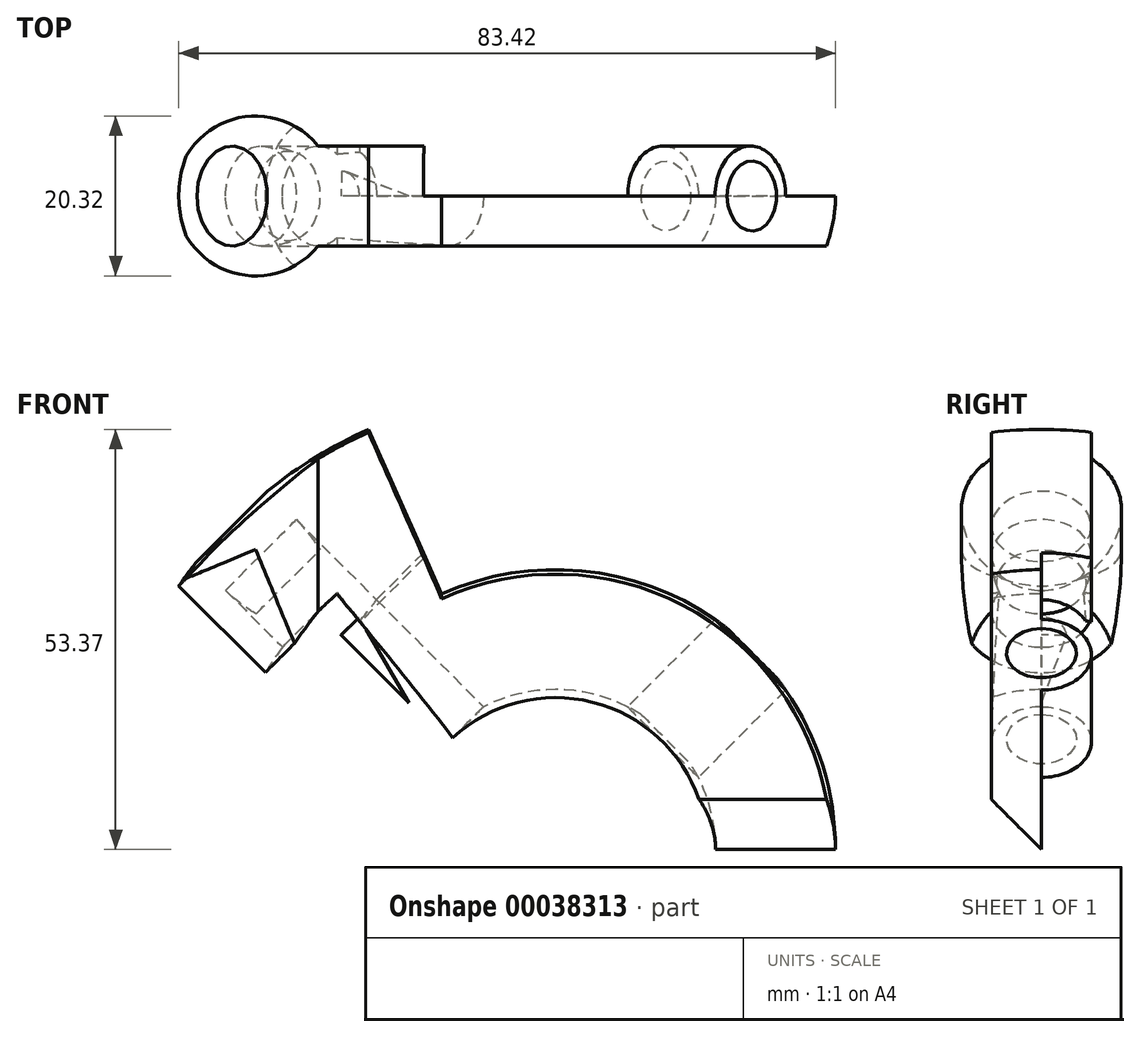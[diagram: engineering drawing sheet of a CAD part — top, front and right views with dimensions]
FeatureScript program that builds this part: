
annotation { "Feature Type Name" : "Feature", "Feature Type Description" : "" }
export const myFeature = defineFeature(function(context is Context, id is Id, definition is map)
    precondition{}
    {
        {
            var Q0;
            Q0=qCreatedBy(makeId("Front.planeOp"),FACE);
            var sketch = newSketch(context, id + "F0", { "sketchPlane" : qUnion([Q0])});
            skArc(sketch, "E0", {"start": v(-26.92, 43.08) * mm, "mid": v(-44.43, 24.63) * mm, "end": v(-50.8, 0) * mm});
            skArc(sketch, "E1.0", {"start": v(-23.76, 53.37) * mm, "mid": v(-49, 31.82) * mm, "end": v(-58.42, 0) * mm});
            skLineSegment(sketch, "E2", {"start": v(-36.32, 0) * mm, "end": v(-50.8, 0) * mm, "construction": true});
            skLineSegment(sketch, "E3", {"start": v(-50.8, 0) * mm, "end": v(48.72, 0) * mm, "construction": true});
            skLineSegment(sketch, "E4", {"start": v(-58.42, 0) * mm, "end": v(-50.8, 0) * mm});
            skLineSegment(sketch, "E5", {"start": v(50.8, 0) * mm, "end": v(58.42, 0) * mm});
            skLineSegment(sketch, "E6", {"start": v(0, 0) * mm, "end": v(0, 35.62) * mm, "construction": true});
            skLineSegment(sketch, "E7", {"start": v(-23.76, 53.37) * mm, "end": v(-14.46, 32.49) * mm});
            skLineSegment(sketch, "E8", {"start": v(-26.92, 43.08) * mm, "end": v(-14.8, 23.7) * mm});
            skArc(sketch, "E9", {"start": v(35.56, 0) * mm, "mid": v(19.37, 29.82) * mm, "end": v(-14.46, 32.49) * mm});
            skArc(sketch, "E10.0", {"start": v(27.94, 0) * mm, "mid": v(13.55, 24.44) * mm, "end": v(-14.8, 23.7) * mm});
            skLineSegment(sketch, "E11", {"start": v(27.94, 0) * mm, "end": v(35.56, 0) * mm});
            skSolve(sketch);
        }
        {
            var Q0;
            Q0=makeQuery(id+"F0.imprint","IMPRINT",FACE,{"disambiguationData":[TD([[makeQuery(id+"F0.imprint","IMPRINT",EDGE,{"derivedFrom":sQuery(id+"F0.wireOp",EDGE,"E0")}),-1.0]])]});
            var Q1;
            Q1=sQuery(id+"F0.wireOp",EDGE,"E3");
            revolve(context, id + "F1", {"entities" : qUnion([Q0]), "axis" : qUnion([Q1]), "revolveType" : RevolveType.SYMMETRIC, "angle" : 90 * degree});
        }
        {
            var Q0;
            Q0=qCreatedBy(makeId("Front.planeOp"),FACE);
            var sketch = newSketch(context, id + "F2", { "sketchPlane" : qUnion([Q0])});
            skArc(sketch, "E12", {"start": v(50.8, 0) * mm, "mid": v(46.93, 19.44) * mm, "end": v(35.92, 35.92) * mm, "construction": true});
            skArc(sketch, "E13.0", {"start": v(43.18, 0) * mm, "mid": v(39.9, 16.52) * mm, "end": v(30.53, 30.53) * mm, "construction": true});
            skLineSegment(sketch, "E14", {"start": v(-50.8, 0) * mm, "end": v(-43.18, 0) * mm});
            skLineSegment(sketch, "E15", {"start": v(43.18, 0) * mm, "end": v(50.8, 0) * mm, "construction": true});
            skLineSegment(sketch, "E16", {"start": v(0, 0) * mm, "end": v(-43.18, 0) * mm, "construction": true});
            skLineSegment(sketch, "E17", {"start": v(0, 0) * mm, "end": v(-64.06, 64.06) * mm, "construction": true});
            skLineSegment(sketch, "E18", {"start": v(0, 0) * mm, "end": v(57.62, 57.62) * mm, "construction": true});
            skLineSegment(sketch, "E19", {"start": v(-26.92, 43.08) * mm, "end": v(-14.8, 23.7) * mm});
            skLineSegment(sketch, "E20", {"start": v(-13.06, 15.57) * mm, "end": v(-27.76, 33.08) * mm});
            skArc(sketch, "E21", {"start": v(27.94, 0) * mm, "mid": v(13.55, 24.44) * mm, "end": v(-14.8, 23.7) * mm});
            skArc(sketch, "E22.0", {"start": v(20.32, 0) * mm, "mid": v(8.59, 18.42) * mm, "end": v(-13.06, 15.57) * mm});
            skLineSegment(sketch, "E23", {"start": v(20.32, 0) * mm, "end": v(27.94, 0) * mm});
            skArc(sketch, "E24.trimOffspring", {"start": v(-27.76, 33.08) * mm, "mid": v(-39.13, 18.25) * mm, "end": v(-43.18, 0) * mm});
            skArc(sketch, "E25.trimOffspring", {"start": v(-26.92, 43.08) * mm, "mid": v(-44.43, 24.63) * mm, "end": v(-50.8, 0) * mm});
            skSolve(sketch);
        }
        {
            var Q0;
            Q0=makeQuery(id+"F2.imprint","IMPRINT",FACE,{"disambiguationData":[TD([[makeQuery(id+"F2.imprint","IMPRINT",EDGE,{"derivedFrom":sQuery(id+"F2.wireOp",EDGE,"E14")}),1.0]])]});
            var Q1;
            Q1=sQuery(id+"F2.wireOp",EDGE,"E16");
            revolve(context, id + "F3", {"entities" : qUnion([Q0]), "axis" : qUnion([Q1]), "revolveType" : RevolveType.SYMMETRIC, "angle" : 90 * degree});
        }
        {
            var Q0;
            Q0=qCreatedBy(makeId("Top.planeOp"),FACE);
            var sketch = newSketch(context, id + "F4", { "sketchPlane" : qUnion([Q0])});
            skLineSegment(sketch, "E26.bottom", {"start": v(50.8, 0) * mm, "end": v(-48.26, 0) * mm, "construction": true});
            skLineSegment(sketch, "E26.top", {"start": v(50.8, 6.35) * mm, "end": v(-30.17, 6.35) * mm});
            skLineSegment(sketch, "E26.left", {"start": v(50.8, 0) * mm, "end": v(50.8, 6.35) * mm});
            skLineSegment(sketch, "E26.right", {"start": v(-48.26, 0) * mm, "end": v(-48.26, 6.35) * mm, "construction": true});
            skLineSegment(sketch, "E27.0.MirrorCS", {"start": v(-48.26, 0) * mm, "end": v(-48.26, -6.35) * mm, "construction": true});
            skLineSegment(sketch, "E28.0.MirrorCS", {"start": v(50.8, -6.35) * mm, "end": v(-30.17, -6.35) * mm});
            skLineSegment(sketch, "E29.0.MirrorCS", {"start": v(50.8, 0) * mm, "end": v(50.8, -6.35) * mm});
            skArc(sketch, "E30", {"start": v(-30.17, 6.35) * mm, "mid": v(-41.46, 9.59) * mm, "end": v(-48.26, 0) * mm});
            skArc(sketch, "E31.0.MirrorCS", {"start": v(-30.17, -6.35) * mm, "mid": v(-41.46, -9.59) * mm, "end": v(-48.26, 0) * mm});
            skSolve(sketch);
        }
        {
            var Q0;
            Q0=makeQuery(id+"F4.imprint","IMPRINT",FACE,{"disambiguationData":[TD([[makeQuery(id+"F4.imprint","IMPRINT",EDGE,{"derivedFrom":sQuery(id+"F4.wireOp",EDGE,"E26.top")}),1.0]])]});
            extrude(context, id + "F5", {"entities" : qUnion([Q0]), "operationType" : NewBodyOperationType.INTERSECT, "endBound" : BoundingType.THROUGH_ALL, "depth" : 25.4 * mm});
        }
        {
            var Q0;
            Q0=sQuery(id+"F2.wireOp",EDGE,"E17");
            cPlane(context, id + "F6", {"entities" : qUnion([Q0]), "cplaneType" : CPlaneType.LINE_ANGLE, "offset" : 152.4 * mm, "angle" : 90 * degree, "width" : 152.4 * mm, "height" : 152.4 * mm});
        }
        {
            var Q0;
            Q0=sQuery(id+"F2.wireOp",EDGE,"E18");
            cPlane(context, id + "F7", {"entities" : qUnion([Q0]), "cplaneType" : CPlaneType.LINE_ANGLE, "offset" : 152.4 * mm, "angle" : 90 * degree, "width" : 152.4 * mm, "height" : 152.4 * mm});
        }
        {
            var Q0;
            Q0=qCreatedBy(id+"F7.planeOp",FACE);
            var sketch = newSketch(context, id + "F8", { "sketchPlane" : qUnion([Q0])});
            skCircle(sketch, "E32", {"center": v(0, 0) * mm, "radius": 6.35 * mm});
            skArc(sketch, "E33", {"start": v(-10.16, 0) * mm, "mid": v(0, -10.16) * mm, "end": v(10.16, 0) * mm});
            skArc(sketch, "E34", {"start": v(-35.56, 0) * mm, "mid": v(0, -35.56) * mm, "end": v(35.56, 0) * mm});
            skLineSegment(sketch, "E35", {"start": v(10.16, 0) * mm, "end": v(35.56, 0) * mm});
            skLineSegment(sketch, "E36", {"start": v(-35.56, 0) * mm, "end": v(-10.16, 0) * mm});
            skSolve(sketch);
        }
        {
            var Q0;
            Q0=makeQuery(id+"F8.imprint","IMPRINT",FACE,{"disambiguationData":[TD([[makeQuery(id+"F8.imprint","IMPRINT",EDGE,{"derivedFrom":sQuery(id+"F8.wireOp",EDGE,"E33")}),-1.0]])]});
            var Q1;
            Q1=makeQuery(id+"F8.imprint","IMPRINT",FACE,{"disambiguationData":[TD([[makeQuery(id+"F8.imprint","IMPRINT",EDGE,{"derivedFrom":sQuery(id+"F8.wireOp",EDGE,"E32")}),1.0]])]});
            extrude(context, id + "F9", {"entities" : qUnion([Q0, Q1]), "operationType" : NewBodyOperationType.REMOVE, "endBound" : BoundingType.THROUGH_ALL, "depth" : 25.4 * mm});
        }
        {
            var Q0;
            Q0=qCreatedBy(makeId("Front.planeOp"),FACE);
            var sketch = newSketch(context, id + "F10", { "sketchPlane" : qUnion([Q0])});
            skLineSegment(sketch, "E37", {"start": v(-36.57, 45.55) * mm, "end": v(-41.06, 41.06) * mm});
            skLineSegment(sketch, "E38", {"start": v(-36.57, 45.55) * mm, "end": v(-32.93, 41.9) * mm});
            skLineSegment(sketch, "E39", {"start": v(-29.94, 38.04) * mm, "end": v(-18.61, 18.61) * mm});
            skLineSegment(sketch, "E40", {"start": v(-18.61, 18.61) * mm, "end": v(-41.06, 41.06) * mm});
            skPoint(sketch, "E41.visualSharp", {"position": v(-31.19, 40.17) * mm});
            skArc(sketch, "E41.filletArc", {"start": v(-29.94, 38.04) * mm, "mid": v(-31.31, 40.07) * mm, "end": v(-32.93, 41.9) * mm});
            skSolve(sketch);
        }
        {
            var Q0;
            Q0=makeQuery(id+"F10.imprint","IMPRINT",FACE,{"disambiguationData":[TD([[makeQuery(id+"F10.imprint","IMPRINT",EDGE,{"derivedFrom":sQuery(id+"F10.wireOp",EDGE,"E37")}),1.0]])]});
            var Q1;
            Q1=sQuery(id+"F2.wireOp",EDGE,"E17");
            revolve(context, id + "F11", {"operationType" : NewBodyOperationType.ADD, "entities" : qUnion([Q0]), "axis" : qUnion([Q1]), "revolveType" : RevolveType.FULL});
        }
        {
            var Q0;
            Q0=qCreatedBy(id+"F6.planeOp",FACE);
            var sketch = newSketch(context, id + "F12", { "sketchPlane" : qUnion([Q0])});
            skCircle(sketch, "E42", {"center": v(0, 0) * mm, "radius": 4.45 * mm});
            skArc(sketch, "E43", {"start": v(0, -6.35) * mm, "mid": v(6.35, 0) * mm, "end": v(0, 6.35) * mm});
            skArc(sketch, "E44", {"start": v(0, -38.52) * mm, "mid": v(38.52, 0) * mm, "end": v(0, 38.52) * mm});
            skLineSegment(sketch, "E45.trimOffspring", {"start": v(0, -6.35) * mm, "end": v(0, -38.52) * mm});
            skLineSegment(sketch, "E46.trimOffspring", {"start": v(0, 6.35) * mm, "end": v(0, 38.52) * mm});
            skSolve(sketch);
        }
        {
            var Q0;
            Q0=makeQuery(id+"F12.imprint","IMPRINT",FACE,{"disambiguationData":[TD([[makeQuery(id+"F12.imprint","IMPRINT",EDGE,{"derivedFrom":sQuery(id+"F12.wireOp",EDGE,"E43")}),-1.0]])]});
            var Q1;
            Q1=makeQuery(id+"F12.imprint","IMPRINT",FACE,{"disambiguationData":[TD([[makeQuery(id+"F12.imprint","IMPRINT",EDGE,{"derivedFrom":sQuery(id+"F12.wireOp",EDGE,"E42")}),1.0]])]});
            extrude(context, id + "F13", {"entities" : qUnion([Q0, Q1]), "operationType" : NewBodyOperationType.REMOVE, "endBound" : BoundingType.THROUGH_ALL, "depth" : 25.4 * mm});
        }
        {
            var Q0;
            Q0=qCreatedBy(id+"F7.planeOp",FACE);
            var sketch = newSketch(context, id + "F14", { "sketchPlane" : qUnion([Q0])});
            skLineSegment(sketch, "E47", {"start": v(0, 19.83) * mm, "end": v(4.45, 19.83) * mm});
            skLineSegment(sketch, "E48", {"start": v(4.45, 35.28) * mm, "end": v(4.45, 19.83) * mm});
            skLineSegment(sketch, "E49", {"start": v(4.45, 35.28) * mm, "end": v(0, 35.28) * mm});
            skLineSegment(sketch, "E50", {"start": v(0, 19.83) * mm, "end": v(0, 35.28) * mm});
            skSolve(sketch);
        }
        {
            var Q0;
            Q0=qSketchRegion(id+"F14",true);
            var Q1;
            Q1=sQuery(id+"F2.wireOp",EDGE,"E18");
            revolve(context, id + "F15", {"operationType" : NewBodyOperationType.ADD, "entities" : qUnion([Q0]), "axis" : qUnion([Q1]), "revolveType" : RevolveType.FULL});
        }
    });
